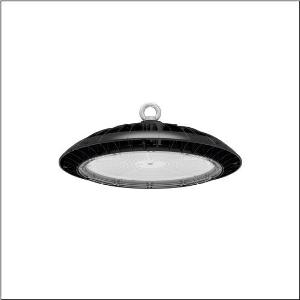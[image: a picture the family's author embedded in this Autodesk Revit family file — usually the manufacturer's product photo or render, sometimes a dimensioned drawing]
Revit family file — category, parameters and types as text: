
# Revit family: highbay_42-l_51hp32mb7mma
name_source: partatom
category: Lighting Fixtures
units: mm (PartAtom-declared; Revit-internal decimal feet)

## family parameters
Cut with Voids When Loaded = No
Host = Face
Light Source = No
Part Type = Normal
Room Calculation Point = No
Round Connector Dimension = Use Diameter
Shared = No

## types (1)
- --- (1 x LED, 28000 lm, 175 W, 5700K)
    Apparent Load = 175 VA
    CIE Flux Codes = 49 82 98 100 100
    Color Rendering = 80
    Color Temperature = 5700K
    Default Elevation = 1800 mm
    Description = Highbay 42-L, high bay luminaire, primary light control with lens, of PC, primary optical cover: cover panel, of PC, transparent, light emission: direct distribution, primary light characteristic: rotationally symmetric, installation type: suspended mounting, surface-mounted, LED, rated luminous flux: 28.000lm, luminous efficacy: 160lm/W, light colour: 857, colour temperature: 5700K, control gear: ON/OFF Multilumen, with cable, 3x 1.0mm², free wire ends, mains connection: 230V, AC, 50Hz, cable length: 1,5m, rated input power: 175W, housing, rotationally symmetric, of diecast aluminium, black, with hook on luminaire side, diameter: 305mm, height: 117mm, protection rating (complete): IP65, insulation class (complete): insulation class I (protective earthing), certification: CE, UKCA, protection symbol: D, impact resistance: IK08, permissible operating ambient temperature: -20..+40°C, corresponds to IFS (International Featured Standards) requirements for safety and quality in the food industry, packaging unit: 1 piece
    Height = 117 mm
    Lamp = 1 x LED
    Lamp Light Flux = 28000 lm
    Lamp Power = 175 W
    Lamp count = 1
    Length = 305 mm
    Luminous efficacy = 160 lm/W
    Manufacturer = Siteco
    ModVariant = No
    Model = 51HP32MB7MMA
    Mounting Place = Ceiling
    Mounting Type = Pendant
    Number of Poles = 1
    OnlyDefault = Yes
    Power Factor = 1
    Product Name = Highbay 42-L
    Product group = high bay luminaire
    ProductGroupID = 902
    Protection Class = Protection class I
    Protection Degree = IP 65
    RLX_Detail_Level = 1
    RLX_Emergency_Light_Flux = 0 lm
    RLX_Emergency_Type = 0
    RLX_Emergency_Type_DB = No
    RlxData = <blob elided: 286281 chars, md5=dd7b640d>
    Socket = socket
    Standby Power = 0 W
    System Light Flux = 28000 lm
    System Power = 175 W
    Type Comments = factory setting: luminous flux: 100 % | (OFF | OFF | OFF)
    Type Image = l_1003932.jpg
    URL = http://relux.com
    VarID = @adj_198739
    Voltage = 0 V
    Weight = 0.00 kg
    Width = 0 mm  [stored 0 ft]

note: [stored X ft] marks values corroborated as IEEE doubles in the binary element streams (Revit-internal decimal feet)

## geometry (parser evidence)
native form markers: Blend x4, Sweep x11
no freeform markers — native parametric forms only
